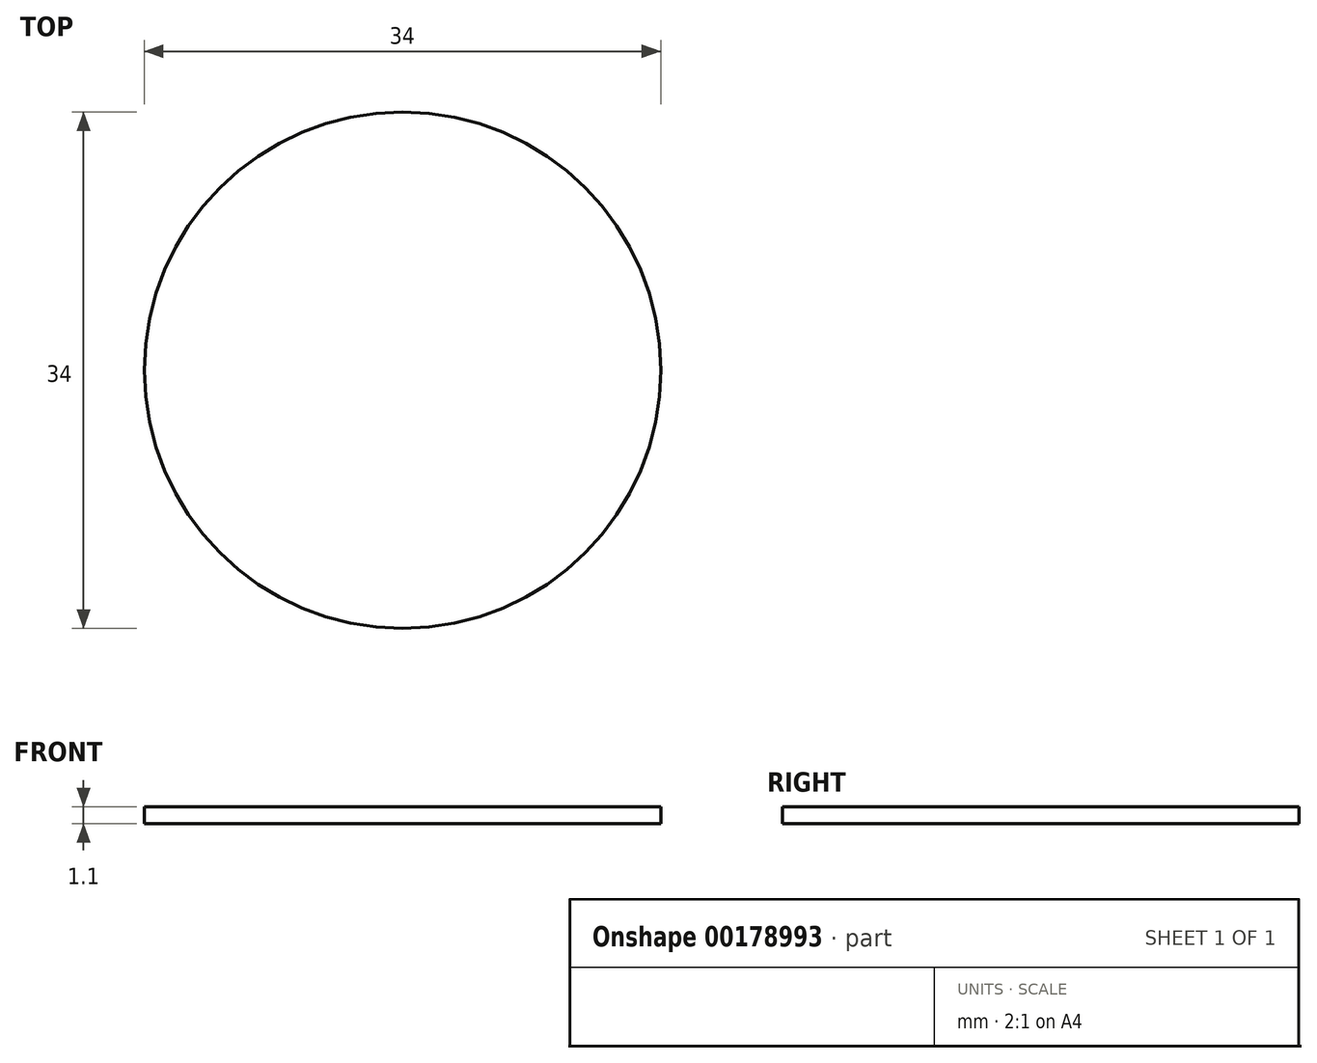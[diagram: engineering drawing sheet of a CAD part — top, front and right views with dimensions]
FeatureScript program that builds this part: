
annotation { "Feature Type Name" : "Feature", "Feature Type Description" : "" }
export const myFeature = defineFeature(function(context is Context, id is Id, definition is map)
    precondition{}
    {
        {
            var Q0;
            Q0=qCreatedBy(makeId("Top.planeOp"),FACE);
            var sketch = newSketch(context, id + "F0", { "sketchPlane" : qUnion([Q0])});
            skCircle(sketch, "E0", {"center": v(0, 0) * mm, "radius": 17 * mm});
            skSolve(sketch);
        }
        {
            var Q0;
            Q0 = qSketchRegion(id + "F0", true);
            extrude(context, id + "F1", {"entities" : qUnion([Q0]), "depth" : 1.1 * mm});
        }
    });
